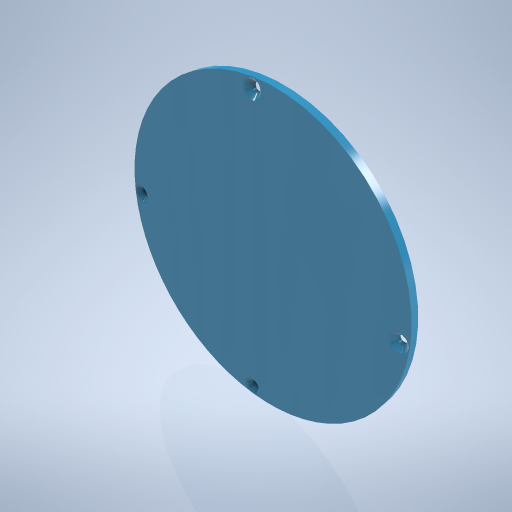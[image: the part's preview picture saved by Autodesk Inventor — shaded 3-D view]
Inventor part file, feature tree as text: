
AUTODESK INVENTOR PART (.ipt)
format: ipt  version: 2024.2 (Build 282272000, 272)  size: 403,968 bytes
history: native  units: mm
features: sketch x2, revolve x1, hole x1
ambient origin geometry x8: Origin, YZ Plane, XZ Plane, XY Plane, X Axis, Y Axis, Z Axis, Center Point
bodies: Volumenkörper1 (feature_tree)
feature tree (4):
  revolve  "Umdrehung1"
  hole  "Bohrung1"  [1 undecoded]
  sketch  "Skizze1"  dims[d0=15.0mm d1=0.5mm]
  sketch  "Skizze2"  dims[d2=60.0deg d3=3.0mm d4=2.0mm d5=90.0mm d7=3.0mm d8=10.0mm d10=10.0mm d12=2.5mm d13=100.0mm d14=20.0mm d15=90.0deg d16=94.0mm d17=94.0mm d18=2.7mm d19=6.0mm d20=5.5mm d21=2.0mm d22=90.0deg d23=8.0mm d24=20.594885mm]
note: 1 required parameter value undecoded (feature->parameter linkage not recoverable at this tier; creation-order binding heuristic only, values carry confidence <= 0.55)
